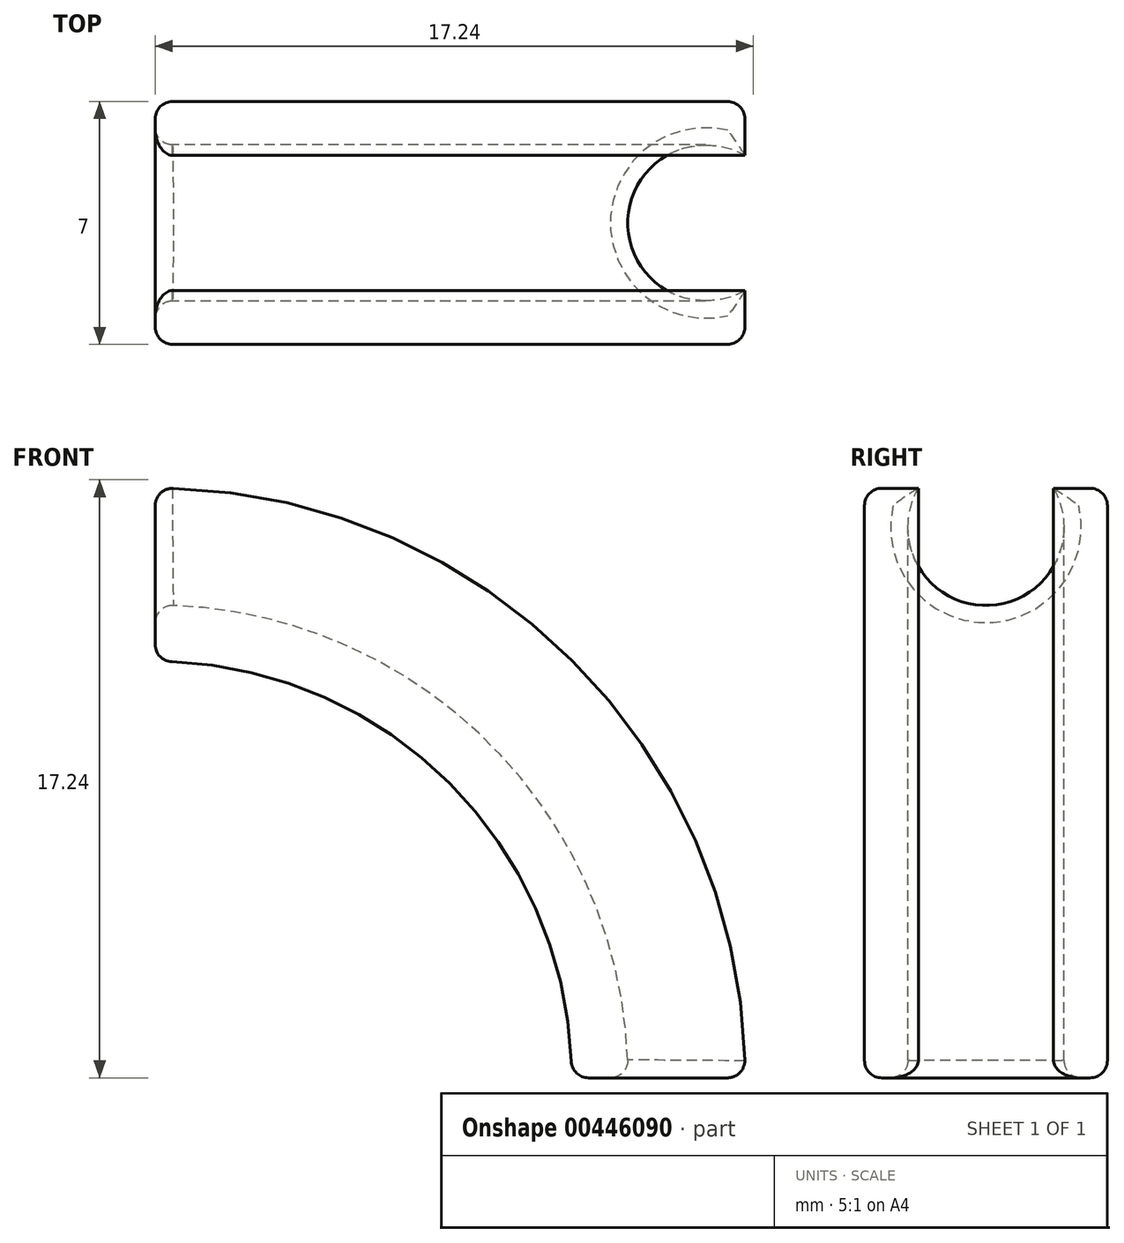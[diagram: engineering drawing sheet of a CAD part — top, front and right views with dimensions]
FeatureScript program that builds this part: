
annotation { "Feature Type Name" : "Feature", "Feature Type Description" : "" }
export const myFeature = defineFeature(function(context is Context, id is Id, definition is map)
    precondition{}
    {
        {
            var Q0;
            Q0=qCreatedBy(makeId("Top.planeOp"),FACE);
            var sketch = newSketch(context, id + "F0", { "sketchPlane" : qUnion([Q0])});
            skPoint(sketch, "E0.middle", {"position": v(0, 0) * mm});
            skCircle(sketch, "E1", {"center": v(15.88, 3.5) * mm, "radius": 2.25 * mm});
            skLineSegment(sketch, "E2.bottom", {"start": v(12, 0) * mm, "end": v(17, 0) * mm});
            skLineSegment(sketch, "E2.top", {"start": v(12, 7) * mm, "end": v(17, 7) * mm});
            skLineSegment(sketch, "E2.left", {"start": v(12, 0) * mm, "end": v(12, 7) * mm});
            skLineSegment(sketch, "E2.right", {"start": v(17, 0) * mm, "end": v(17, 7) * mm});
            skSolve(sketch);
        }
        {
            var Q0;
            Q0=qCreatedBy(makeId("Front.planeOp"),FACE);
            var sketch = newSketch(context, id + "F1", { "sketchPlane" : qUnion([Q0])});
            skArc(sketch, "E3", {"start": v(17, 0) * mm, "mid": v(12.02, 12.02) * mm, "end": v(0, 17) * mm});
            skSolve(sketch);
        }
        {
            var Q0;
            {var subQ1=sQuery(id+"F0.wireOp",EDGE,"E2.bottom");Q0=makeQuery(id+"F0.imprint","IMPRINT",FACE,{"disambiguationData":[TD([[makeQuery(id+"F0.imprint","IMPRINT",EDGE,{"derivedFrom":subQ1}),1.0]])]});}
            var Q1;
            Q1=sQuery(id+"F1.wireOp",EDGE,"E3");
            sweep(context, id + "F2", {"profiles" : qUnion([Q0]), "path" : qUnion([Q1])});
        }
        {
            var Q0;
            Q0=makeQuery(id+"F2.opSweep","SWEPT_FACE",FACE,{"disambiguationData":[OSD([sQuery(id+"F0.wireOp",EDGE,"E2.left"),sQuery(id+"F1.wireOp",EDGE,"E3")])]});
            var Q1;
            Q1=makeQuery(id+"F2.opSweep","CAP_FACE",FACE,{"disambiguationData":[OSD([sQuery(id+"F0.wireOp",EDGE,"E1"),sQuery(id+"F0.wireOp",EDGE,"E2.bottom"),sQuery(id+"F0.wireOp",EDGE,"E2.top"),sQuery(id+"F0.wireOp",EDGE,"E2.left"),sQuery(id+"F0.wireOp",EDGE,"E2.right"),sQuery(id+"F1.wireOp",VERTEX,"E3.start")])],"isStart":true});
            var Q2;
            Q2=makeQuery(id+"F2.opSweep","CAP_FACE",FACE,{"disambiguationData":[OSD([sQuery(id+"F0.wireOp",EDGE,"E1"),sQuery(id+"F0.wireOp",EDGE,"E2.bottom"),sQuery(id+"F0.wireOp",EDGE,"E2.top"),sQuery(id+"F0.wireOp",EDGE,"E2.left"),sQuery(id+"F0.wireOp",EDGE,"E2.right"),sQuery(id+"F1.wireOp",VERTEX,"E3.end")])],"isStart":false});
            var Q3;
            Q3=makeQuery(id+"F2.opSweep","SWEPT_EDGE",EDGE,{"disambiguationData":[OSD([sQuery(id+"F0.wireOp",EDGE,"E2.top"),sQuery(id+"F0.wireOp",EDGE,"E2.right"),sQuery(id+"F1.wireOp",EDGE,"E3")])]});
            var Q4;
            Q4=makeQuery(id+"F2.opSweep","SWEPT_EDGE",EDGE,{"disambiguationData":[OSD([sQuery(id+"F0.wireOp",EDGE,"E2.bottom"),sQuery(id+"F0.wireOp",EDGE,"E2.right"),sQuery(id+"F1.wireOp",EDGE,"E3")])]});
            fillet(context, id + "F3", {"entities" : qUnion([Q0, Q1, Q2, Q3, Q4]), "radius" : .5 * mm, "tangentPropagation" : true, "allowEdgeOverflow" : false});
        }
    });
